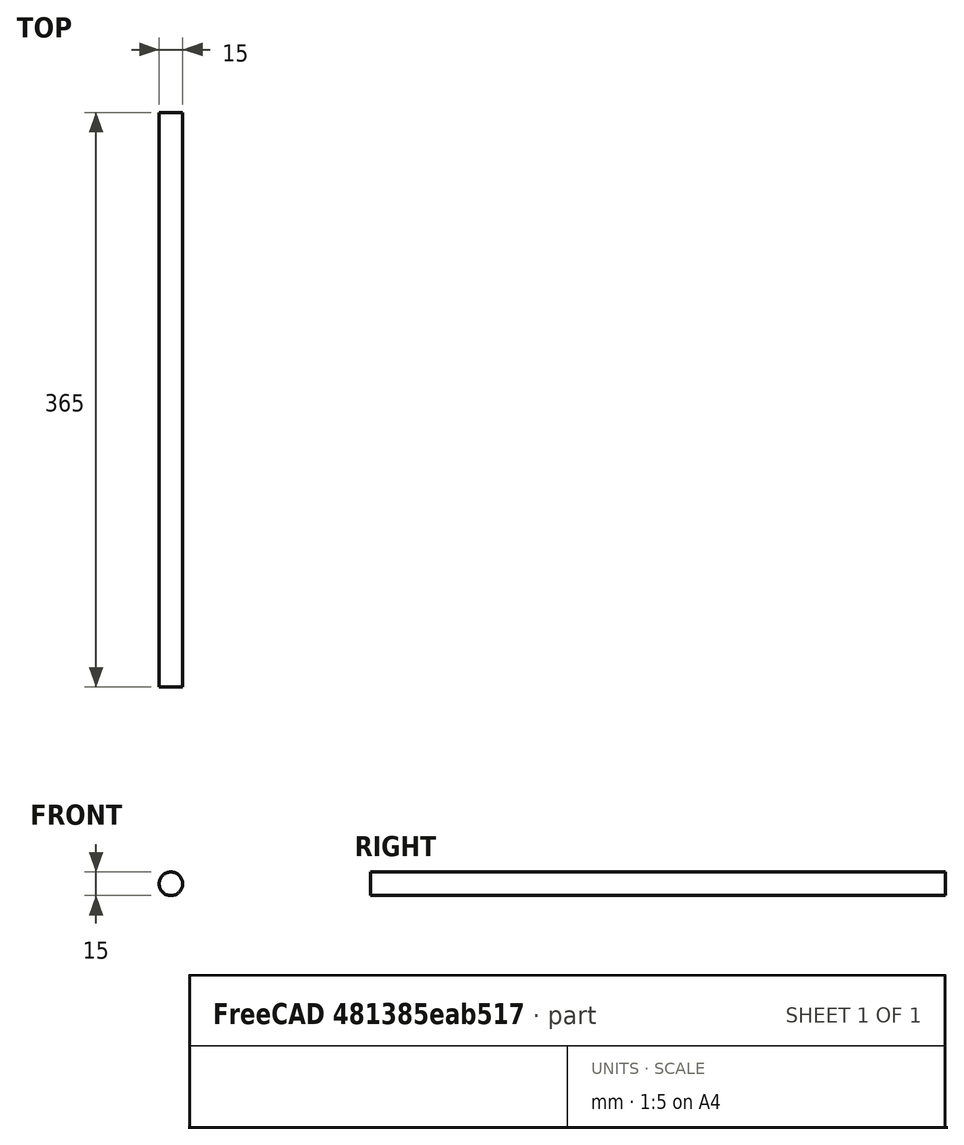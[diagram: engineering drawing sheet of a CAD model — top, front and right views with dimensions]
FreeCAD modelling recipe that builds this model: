
FCSTD DOCUMENT  (FreeCAD 0.21R33771 (Git))
Label: y screw rod
License: All rights reserved
LicenseURL: http://en.wikipedia.org/wiki/All_rights_reserved
objects: Sketcher::SketchObject×1, PartDesign::Pad×1, PartDesign::Body×1
note: 4 computed .brp shape members not serialized (recipe doc carries the construction recipe); baked Part::Feature solids carry a one-line shape summary decoded from their .brp

FEATURE [Sketcher::SketchObject] Sketch
  FullyConstrained = true
  MapMode = 5
  Placement = pos=(0,0,0) rot=(1,0,0;1.5708rad)
  Support = -> [XZ_Plane]
  sketch-geometry (1):
    g0: Circle CenterX=0 CenterY=0 CenterZ=0 NormalX=0 NormalY=0 NormalZ=1 AngleXU=0 Radius=7.5
  constraints (2):
    c: Coincident(g0,g-1)
    c: Radius(g0) = 7.5
FEATURE [PartDesign::Pad] Pad
  Direction = (0,-1,2e-16)
  Length = 365
  Length2 = 10
  Placement = pos=(0,0,0) rot=(1,0,0;1.5708rad)
  Profile = -> Sketch
  ReferenceAxis = -> Sketch [N_Axis]
  Type = 0
FEATURE [PartDesign::Body] Body
  Group = -> [Sketch,Pad]
  Origin = -> Origin
  Tip = -> Pad
